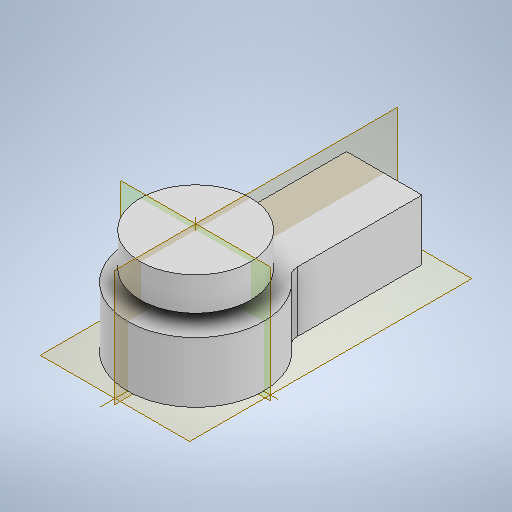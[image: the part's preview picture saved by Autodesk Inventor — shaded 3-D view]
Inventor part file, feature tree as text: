
AUTODESK INVENTOR PART (.ipt)
format: ipt  version: 2025.1 (Build 291241000, 241)  size: 279,040 bytes
history: native  units: mm
features: sketch x2, extrude x1, revolve x1
ambient origin geometry x8: Origin, YZ Plane, XZ Plane, XY Plane, X Axis, Y Axis, Z Axis, Center Point
bodies: Body1 (feature_tree)
feature tree (4):
  extrude  "Extrusion1"  TaperAngle=0.0deg  [1 undecoded]
  revolve  "Umdrehung1"
  sketch  "Skizze1"  dims[d1=18.0mm d2=5.0mm d3=2.0mm d4=4.0mm d5=10.0mm d6=5.0mm d7=0.0mm d8=25.0mm d9=0.0mm]
  sketch  "Skizze3"  dims[d10=0.0mm d11=8.0mm d12=0.0mm d13=6.0mm d14=4.9mm d15=1.2mm d16=1.2mm d17=1.6mm d18=2.8mm d19=90.0deg]
note: 1 required parameter value undecoded (feature->parameter linkage not recoverable at this tier; creation-order binding heuristic only, values carry confidence <= 0.55)
